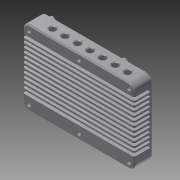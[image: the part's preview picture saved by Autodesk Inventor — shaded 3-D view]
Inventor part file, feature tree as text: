
AUTODESK INVENTOR PART (.ipt)
format: ipt  version: 2013 SP2 (Build 170200200, 200)  size: 322,560 bytes
history: native  units: mm
features: sketch x7, extrude x4, hole x3, projected_geometry x3, fillet x1, chamfer x1, plane x1, mirror x1
ambient origin geometry x8: Origin, YZ Plane, XZ Plane, XY Plane, X Axis, Y Axis, Z Axis, Center Point
bodies: Solid1 (feature_tree)
feature tree (21):
  extrude  "Extrusion1"  Depth=56.0mm
  fillet  "Fillet1"  Radius=1.5mm
  extrude  "Extrusion2"  Depth=2.0mm
  extrude  "Extrusion3"  Depth=5.0mm
  hole  "Hole1"  [1 undecoded]
  chamfer  "Chamfer1"  Distance=5.0mm
  hole  "Hole2"  [1 undecoded]
  hole  "Hole3"  [1 undecoded]
  plane  "Work Plane1"
  mirror  "Mirror1"
  extrude  "Extrusion4"  Depth=5.0mm
  sketch  "Sketch1"  dims[d0=85.0mm d2=56.0mm d3=1.5mm d4=0.0mm]
  sketch  "Sketch2"  dims[d5=3.0mm d6=2.0mm]
  sketch  "Sketch3"  dims[d7=14.0mm d8=0.0mm d9=5.0mm]
  sketch  "Sketch4"  dims[d10=3.5mm d11=3.5mm]
  projected_geometry  "Projected Loop1"
  projected_geometry  "Projected Loop2"
  projected_geometry  "Projected Loop3"
  sketch  "Sketch5"  dims[d12=5.0mm]
  sketch  "Sketch6"  dims[d13=3.5mm]
  sketch  "Sketch7"  dims[d14=58.0mm d15=5.0mm d16=3.5mm d17=3.5mm d18=5.0mm d19=58.0mm d20=3.5mm d21=3.0mm d22=0.0mm d23=3.0mm d24=6.0mm d25=4.0mm d26=2.0mm d27=90.0deg d28=7.0mm d29=0.0mm d30=1.0mm d31=2.0mm d32=45.0deg d33=3.0mm d34=6.0mm d35=3.5mm d36=2.0mm d37=90.0deg d38=4.5mm d39=0.0mm d40=70.0mm d42=10.0mm d43=10.0mm d45=10.0mm d47=5.0mm d48=6.0mm d49=6.2mm d50=2.0mm d51=90.0deg d52=8.0mm d53=0.0mm d55=2.0mm d58=100.0mm d60=3.5mm d61=10.0mm d63=10.0mm d65=13.0mm d66=0.0mm d72=2.5mm d74=1.3mm d75=1.3mm d76=2.5mm d77=49.0mm d78=30.0mm d80=40.0mm d81=20.0mm d83=51.0mm]
note: 3 required parameter values undecoded (feature->parameter linkage not recoverable at this tier; creation-order binding heuristic only, values carry confidence <= 0.55)
